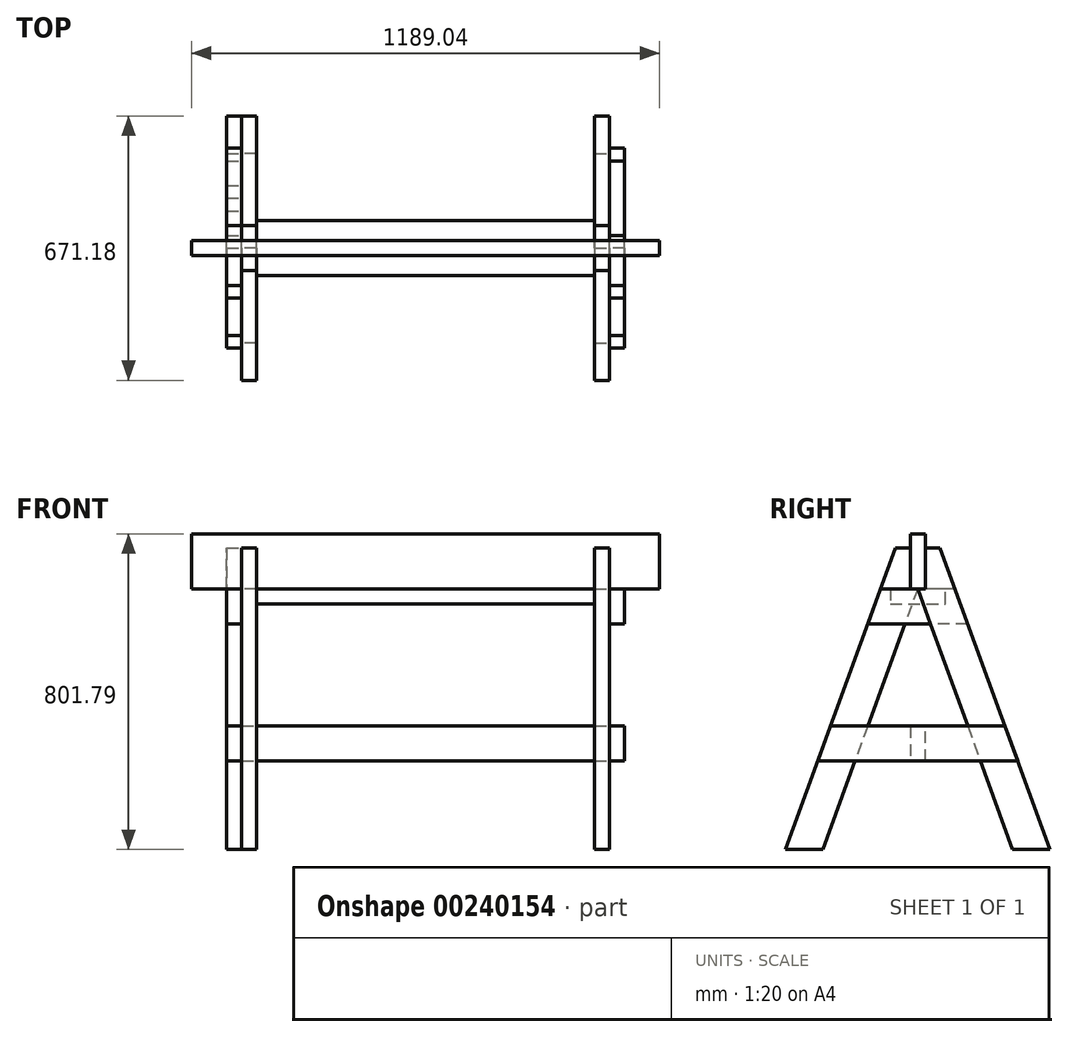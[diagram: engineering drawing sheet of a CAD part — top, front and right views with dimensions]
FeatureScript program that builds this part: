
annotation { "Feature Type Name" : "Feature", "Feature Type Description" : "" }
export const myFeature = defineFeature(function(context is Context, id is Id, definition is map)
    precondition{}
    {
        {
            var Q0;
            Q0=qCreatedBy(makeId("Right.planeOp"),FACE);
            var sketch = newSketch(context, id + "F0", { "sketchPlane" : qUnion([Q0])});
            skLineSegment(sketch, "E0", {"start": v(-19.05, -69.85) * mm, "end": v(-19.05, 69.85) * mm});
            skLineSegment(sketch, "E1", {"start": v(-19.05, 69.85) * mm, "end": v(19.05, 69.85) * mm});
            skLineSegment(sketch, "E2", {"start": v(19.05, 69.85) * mm, "end": v(19.05, -69.85) * mm});
            skLineSegment(sketch, "E3", {"start": v(19.05, -69.85) * mm, "end": v(-19.05, -69.85) * mm});
            skPoint(sketch, "E4", {"position": v(19.05, 0) * mm});
            skPoint(sketch, "E5", {"position": v(0, -69.85) * mm});
            skPoint(sketch, "E6", {"position": v(0, 69.85) * mm});
            skPoint(sketch, "E7", {"position": v(-19.05, 0) * mm});
            skSolve(sketch);
        }
        {
            var Q0;
            Q0 = qSketchRegion(id + "F0", true);
            extrude(context, id + "F1", {"entities" : qUnion([Q0]), "endBound" : BoundingType.SYMMETRIC, "depth" : 1189.04 * mm});
        }
        {
            var Q0;
            Q0=makeQuery(id+"F1.opExtrude","CAP_FACE",FACE,{"disambiguationData":[OSD([sQuery(id+"F0.wireOp",EDGE,"E0"),sQuery(id+"F0.wireOp",EDGE,"E1"),sQuery(id+"F0.wireOp",EDGE,"E2"),sQuery(id+"F0.wireOp",EDGE,"E3")])],"isStart":true});
            cPlane(context, id + "F2", {"entities" : qUnion([Q0]), "cplaneType" : CPlaneType.OFFSET, "offset" : 127 * mm, "oppositeDirection" : true, "width" : 152.4 * mm, "height" : 152.4 * mm});
        }
        {
            var Q0;
            Q0=qCreatedBy(id+"F2.planeOp",FACE);
            var sketch = newSketch(context, id + "F3", { "sketchPlane" : qUnion([Q0])});
            skLineSegment(sketch, "E8.0", {"start": v(19.05, 69.85) * mm, "end": v(-19.05, 69.85) * mm, "construction": true});
            skLineSegment(sketch, "E9.0", {"start": v(-19.05, 69.85) * mm, "end": v(-19.05, -69.85) * mm, "construction": true});
            skLineSegment(sketch, "E10.0", {"start": v(-19.05, -69.85) * mm, "end": v(19.05, -69.85) * mm, "construction": true});
            skLineSegment(sketch, "E11.0", {"start": v(19.05, -69.85) * mm, "end": v(19.05, 69.85) * mm, "construction": true});
            skLineSegment(sketch, "E12", {"start": v(0, -69.85) * mm, "end": v(0, -731.84) * mm, "construction": true});
            skLineSegment(sketch, "E13", {"start": v(0, -69.85) * mm, "end": v(240.98, -731.94) * mm});
            skLineSegment(sketch, "E14", {"start": v(0, -69.85) * mm, "end": v(19.05, -69.85) * mm});
            skLineSegment(sketch, "E15", {"start": v(19.05, -69.85) * mm, "end": v(19.05, 33.34) * mm});
            skLineSegment(sketch, "E16", {"start": v(19.05, 33.34) * mm, "end": v(57.05, 33.34) * mm});
            skLineSegment(sketch, "E17", {"start": v(57.05, 33.34) * mm, "end": v(335.59, -731.94) * mm});
            skLineSegment(sketch, "E18", {"start": v(335.59, -731.94) * mm, "end": v(240.98, -731.94) * mm});
            skLineSegment(sketch, "E19", {"start": v(57.05, 33.34) * mm, "end": v(0, 190.08) * mm, "construction": true});
            skLineSegment(sketch, "E20", {"start": v(0, 69.85) * mm, "end": v(0, 190.08) * mm, "construction": true});
            skSolve(sketch);
        }
        {
            var Q0;
            Q0 = qSketchRegion(id + "F3", true);
            extrude(context, id + "F4", {"entities" : qUnion([Q0]), "oppositeDirection" : true, "depth" : 38.1 * mm});
        }
        {
            var Q0;
            Q0=makeQuery(id+"F4.opExtrude","SWEPT_BODY",BODY,{"disambiguationData":[OSD([sQuery(id+"F3.wireOp",EDGE,"E13"),sQuery(id+"F3.wireOp",EDGE,"E14"),sQuery(id+"F3.wireOp",EDGE,"E15"),sQuery(id+"F3.wireOp",EDGE,"E16"),sQuery(id+"F3.wireOp",EDGE,"E17"),sQuery(id+"F3.wireOp",EDGE,"E18")])]});
            var Q1;
            Q1=qCreatedBy(makeId("Right.planeOp"),FACE);
            mirror(context, id + "F5", {"entities" : qUnion([Q0]), "mirrorPlane" : qUnion([Q1])});
        }
        {
            var Q0;
            Q0=makeQuery(id+"F4.opExtrude","SWEPT_BODY",BODY,{"disambiguationData":[OSD([sQuery(id+"F3.wireOp",EDGE,"E13"),sQuery(id+"F3.wireOp",EDGE,"E14"),sQuery(id+"F3.wireOp",EDGE,"E15"),sQuery(id+"F3.wireOp",EDGE,"E16"),sQuery(id+"F3.wireOp",EDGE,"E17"),sQuery(id+"F3.wireOp",EDGE,"E18")])]});
            var Q1;
            Q1=makeQuery(id+"F5.opPattern","COPY",BODY,{"derivedFrom":makeQuery(id+"F4.opExtrude","SWEPT_BODY",BODY,{"disambiguationData":[OSD([sQuery(id+"F3.wireOp",EDGE,"E13"),sQuery(id+"F3.wireOp",EDGE,"E14"),sQuery(id+"F3.wireOp",EDGE,"E15"),sQuery(id+"F3.wireOp",EDGE,"E16"),sQuery(id+"F3.wireOp",EDGE,"E17"),sQuery(id+"F3.wireOp",EDGE,"E18")])]}),"instanceName":"1"});
            var Q2;
            Q2=qCreatedBy(makeId("Front.planeOp"),FACE);
            mirror(context, id + "F6", {"entities" : qUnion([Q0, Q1]), "mirrorPlane" : qUnion([Q2])});
        }
        {
            var Q0;
            Q0=makeQuery(id+"F6.opPattern","COPY",FACE,{"derivedFrom":makeQuery(id+"F4.opExtrude","CAP_FACE",FACE,{"disambiguationData":[OSD([sQuery(id+"F3.wireOp",EDGE,"E13"),sQuery(id+"F3.wireOp",EDGE,"E14"),sQuery(id+"F3.wireOp",EDGE,"E15"),sQuery(id+"F3.wireOp",EDGE,"E16"),sQuery(id+"F3.wireOp",EDGE,"E17"),sQuery(id+"F3.wireOp",EDGE,"E18")])],"isStart":true}),"instanceName":"1"});
            var sketch = newSketch(context, id + "F7", { "sketchPlane" : qUnion([Q0])});
            skPoint(sketch, "E21.0", {"position": v(0, -69.85) * mm});
            skLineSegment(sketch, "E22.0", {"start": v(-57.05, 33.34) * mm, "end": v(-335.59, -731.94) * mm});
            skLineSegment(sketch, "E23.0", {"start": v(57.05, 33.34) * mm, "end": v(335.59, -731.94) * mm});
            skLineSegment(sketch, "E24", {"start": v(-94.6, -69.85) * mm, "end": v(94.6, -69.85) * mm});
            skLineSegment(sketch, "E25.0", {"start": v(-126.96, -158.75) * mm, "end": v(126.96, -158.75) * mm});
            skLineSegment(sketch, "E26", {"start": v(-126.96, -158.75) * mm, "end": v(-94.6, -69.85) * mm});
            skLineSegment(sketch, "E27", {"start": v(94.6, -69.85) * mm, "end": v(126.96, -158.75) * mm});
            skLineSegment(sketch, "E28", {"start": v(254, -507.78) * mm, "end": v(-254, -507.78) * mm});
            skLineSegment(sketch, "E29.0", {"start": v(221.64, -418.88) * mm, "end": v(-221.64, -418.88) * mm});
            skLineSegment(sketch, "E30", {"start": v(-221.64, -418.88) * mm, "end": v(-254, -507.78) * mm});
            skLineSegment(sketch, "E31", {"start": v(221.64, -418.88) * mm, "end": v(254, -507.78) * mm});
            skSolve(sketch);
        }
        {
            var Q0;
            {var subQ0=sQuery(id+"F7.wireOp",EDGE,"E26");Q0=makeQuery(id+"F7.imprint","IMPRINT",FACE,{"disambiguationData":[TD([[makeQuery(id+"F7.imprint","IMPRINT",EDGE,{"derivedFrom":subQ0}),1.0]])]});}
            var Q1;
            {var subQ3=sQuery(id+"F7.wireOp",EDGE,"E27");Q1=makeQuery(id+"F7.imprint","IMPRINT",FACE,{"disambiguationData":[TD([[makeQuery(id+"F7.imprint","IMPRINT",EDGE,{"derivedFrom":subQ3}),-1.0]])]});}
            extrude(context, id + "F8", {"entities" : qUnion([Q0, Q1]), "depth" : 38.1 * mm});
        }
        {
            var Q0;
            {var subQ0=sQuery(id+"F7.wireOp",EDGE,"E30");Q0=makeQuery(id+"F7.imprint","IMPRINT",FACE,{"disambiguationData":[TD([[makeQuery(id+"F7.imprint","IMPRINT",EDGE,{"derivedFrom":subQ0}),1.0]])]});}
            var Q1;
            {var subQ0=sQuery(id+"F7.wireOp",EDGE,"E31");Q1=makeQuery(id+"F7.imprint","IMPRINT",FACE,{"disambiguationData":[TD([[makeQuery(id+"F7.imprint","IMPRINT",EDGE,{"derivedFrom":subQ0}),-1.0]])]});}
            extrude(context, id + "F9", {"entities" : qUnion([Q0, Q1]), "depth" : 38.1 * mm});
        }
        {
            var Q0;
            Q0=makeQuery(id+"F8.opExtrude","SWEPT_BODY",BODY,{"disambiguationData":[OSD([sQuery(id+"F7.wireOp",EDGE,"E24"),sQuery(id+"F7.wireOp",EDGE,"E25.0"),sQuery(id+"F7.wireOp",EDGE,"E26"),sQuery(id+"F7.wireOp",EDGE,"E27")])]});
            var Q1;
            Q1=makeQuery(id+"F9.opExtrude","SWEPT_BODY",BODY,{"disambiguationData":[OSD([sQuery(id+"F7.wireOp",EDGE,"E28"),sQuery(id+"F7.wireOp",EDGE,"E29.0"),sQuery(id+"F7.wireOp",EDGE,"E30"),sQuery(id+"F7.wireOp",EDGE,"E31")])]});
            var Q2;
            Q2=qCreatedBy(makeId("Right.planeOp"),FACE);
            mirror(context, id + "F10", {"entities" : qUnion([Q0, Q1]), "mirrorPlane" : qUnion([Q2])});
        }
        {
            var Q0;
            Q0=makeQuery(id+"F6.opPattern","COPY",FACE,{"derivedFrom":makeQuery(id+"F5.opPattern","COPY",FACE,{"derivedFrom":makeQuery(id+"F4.opExtrude","CAP_FACE",FACE,{"disambiguationData":[OSD([sQuery(id+"F3.wireOp",EDGE,"E13"),sQuery(id+"F3.wireOp",EDGE,"E14"),sQuery(id+"F3.wireOp",EDGE,"E15"),sQuery(id+"F3.wireOp",EDGE,"E16"),sQuery(id+"F3.wireOp",EDGE,"E17"),sQuery(id+"F3.wireOp",EDGE,"E18")])],"isStart":false}),"instanceName":"1"}),"instanceName":"1"});
            var sketch = newSketch(context, id + "F11", { "sketchPlane" : qUnion([Q0])});
            skPoint(sketch, "E32.0", {"position": v(0, -69.85) * mm});
            skLineSegment(sketch, "E33", {"start": v(-69.85, -69.85) * mm, "end": v(69.85, -69.85) * mm});
            skLineSegment(sketch, "E34", {"start": v(69.85, -69.85) * mm, "end": v(69.85, -107.95) * mm});
            skLineSegment(sketch, "E35", {"start": v(69.85, -107.95) * mm, "end": v(-69.85, -107.95) * mm});
            skLineSegment(sketch, "E36", {"start": v(-69.85, -107.95) * mm, "end": v(-69.85, -69.85) * mm});
            skPoint(sketch, "E36.endSnap0", {"position": v(-9.52, -69.85) * mm});
            skSolve(sketch);
        }
        {
            var Q0;
            Q0 = qSketchRegion(id + "F11", true);
            var Q1;
            Q1=makeQuery(id+"F6.opPattern","COPY",FACE,{"derivedFrom":makeQuery(id+"F4.opExtrude","CAP_FACE",FACE,{"disambiguationData":[OSD([sQuery(id+"F3.wireOp",EDGE,"E13"),sQuery(id+"F3.wireOp",EDGE,"E14"),sQuery(id+"F3.wireOp",EDGE,"E15"),sQuery(id+"F3.wireOp",EDGE,"E16"),sQuery(id+"F3.wireOp",EDGE,"E17"),sQuery(id+"F3.wireOp",EDGE,"E18")])],"isStart":false}),"instanceName":"1"});
            var Q2;
            Q2=makeQuery(id+"F6.opPattern","COPY",BODY,{"derivedFrom":makeQuery(id+"F4.opExtrude","SWEPT_BODY",BODY,{"disambiguationData":[OSD([sQuery(id+"F3.wireOp",EDGE,"E13"),sQuery(id+"F3.wireOp",EDGE,"E14"),sQuery(id+"F3.wireOp",EDGE,"E15"),sQuery(id+"F3.wireOp",EDGE,"E16"),sQuery(id+"F3.wireOp",EDGE,"E17"),sQuery(id+"F3.wireOp",EDGE,"E18")])]}),"instanceName":"1"});
            extrude(context, id + "F12", {"entities" : qUnion([Q0]), "endBound" : BoundingType.UP_TO_SURFACE, "endBoundEntityFace" : qUnion([Q1]), "endBoundEntityBody" : qUnion([Q2]), "depth" : 25.4 * mm});
        }
        {
            var Q0;
            Q0=makeQuery(id+"F10.opPattern","COPY",FACE,{"derivedFrom":makeQuery(id+"F9.opExtrude","CAP_FACE",FACE,{"disambiguationData":[OSD([sQuery(id+"F7.wireOp",EDGE,"E28"),sQuery(id+"F7.wireOp",EDGE,"E29.0"),sQuery(id+"F7.wireOp",EDGE,"E30"),sQuery(id+"F7.wireOp",EDGE,"E31")])],"isStart":true}),"instanceName":"1"});
            var sketch = newSketch(context, id + "F13", { "sketchPlane" : qUnion([Q0])});
            skPoint(sketch, "E37.0", {"position": v(0, -418.88) * mm});
            skLineSegment(sketch, "E38", {"start": v(-19.05, -418.88) * mm, "end": v(19.05, -418.88) * mm});
            skLineSegment(sketch, "E39", {"start": v(19.05, -418.88) * mm, "end": v(19.05, -507.78) * mm});
            skLineSegment(sketch, "E40", {"start": v(19.05, -507.78) * mm, "end": v(-19.05, -507.78) * mm});
            skLineSegment(sketch, "E41", {"start": v(-19.05, -507.78) * mm, "end": v(-19.05, -418.88) * mm});
            skSolve(sketch);
        }
        {
            var Q0;
            Q0=makeQuery(id+"F13.imprint","IMPRINT",FACE,{"disambiguationData":[TD([[makeQuery(id+"F13.imprint","IMPRINT",EDGE,{"derivedFrom":sQuery(id+"F13.wireOp",EDGE,"E38")}),1.0]])]});
            var Q1;
            Q1=makeQuery(id+"F9.opExtrude","CAP_FACE",FACE,{"disambiguationData":[OSD([sQuery(id+"F7.wireOp",EDGE,"E28"),sQuery(id+"F7.wireOp",EDGE,"E29.0"),sQuery(id+"F7.wireOp",EDGE,"E30"),sQuery(id+"F7.wireOp",EDGE,"E31")])],"isStart":true});
            extrude(context, id + "F14", {"entities" : qUnion([Q0]), "endBound" : BoundingType.UP_TO_SURFACE, "endBoundEntityFace" : qUnion([Q1]), "depth" : 25.4 * mm});
        }
    });
